# Revit family: kawneer-flushline_novl-pr_20636
name_source: partatom
category: Doors
revit_build: Autodesk Revit 2015 (Build: 20140905_0730(x64)
units: mm (PartAtom-declared; Revit-internal decimal feet)

## types (1)
- kawneer-flushline_novl-pr_20636
    2-Color Option = no
    Air Infiltration (ASTM E 283) = product not tested
    Application = moderate traffic, high traffic, impact areas
    Assembly Code = B2030110
    CSI Masterformat Code = 08 41 13
    Color = any
    Depth = 0 mm  [stored 0 ft]
    Description = The "Flushline" entrance is a polyurethane foam filled door with FRP or aluminum face sheets designed in various textures for interior or exterior use.
    Door Corner Construction = Welded
    Door Handle Material = <By Category>
    Door Opening = 0 mm  [stored 0 ft]
    Door Panel Height = 0 mm  [stored 0 ft]
    Door Panel Material = <By Category>
    Door Panel Width = 0 mm  [stored 0 ft]
    Function = Interior
    Function (Interior or Exterior) = Exterior, Interior
    Glass Capture = Captured
    Glass Installtion = cut outs for vision area, inside or outside
    Glass U-Factor = product not tested
    Glazing Thickness = 0 mm  [stored 0 ft]
    Hinging Types = Offset Pivot, Butt Hinge, Continuous Gear Hinge
    Hurricane Resistant Tested = product not tested
    Keywords = Entrance, Door, Swing Door, FRP Skin Door, Aluminum Skin Door, Foam-filled Door
    Manufacturer = Kawneer
    Manufacturer Part Number = Flushline®
    Model = Flushline®
    Overall U-Factor = product not tested
    Panel Inserts Material = <By Category>
    Product data url = https://bimobject.com
    Short Description = Foam-filled with Aluminum or FRP Face Sheets
    Sightline = 0 mm  [stored 0 ft]
    Thermal Transmittance = < 0.28 BTU/hr/sf/F
    Thickness = 0 mm  [stored 0 ft]
    Type Comments = Foam-filled with Aluminum or FRP Face Sheets
    Type of Glazing = monolithic, insulating
    URL = http://www.kawneer.com
    Water - Static (ASTM E 331) = product not tested
    Width = 0 mm  [stored 0 ft]

note: [stored X ft] marks values corroborated as IEEE doubles in the binary element streams (Revit-internal decimal feet)

## geometry (parser evidence)
native form markers: Sweep x12
no freeform markers — native parametric forms only
